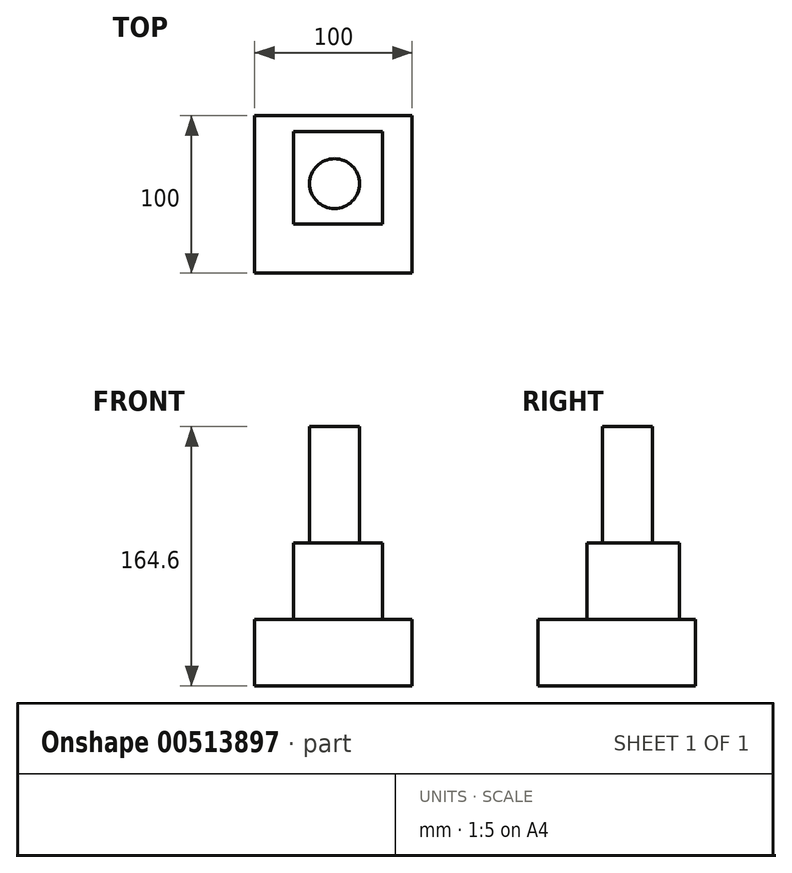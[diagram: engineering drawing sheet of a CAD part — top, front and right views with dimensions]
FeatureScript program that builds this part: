
annotation { "Feature Type Name" : "Feature", "Feature Type Description" : "" }
export const myFeature = defineFeature(function(context is Context, id is Id, definition is map)
    precondition{}
    {
        {
            var Q0;
            Q0=qCreatedBy(makeId("Top.planeOp"),FACE);
            var sketch = newSketch(context, id + "F0", { "sketchPlane" : qUnion([Q0])});
            skLineSegment(sketch, "E0.bottom", {"start": v(-50.73, 47.1) * mm, "end": v(49.27, 47.1) * mm});
            skLineSegment(sketch, "E0.top", {"start": v(-50.73, -52.9) * mm, "end": v(49.27, -52.9) * mm});
            skLineSegment(sketch, "E0.left", {"start": v(-50.73, 47.1) * mm, "end": v(-50.73, -52.9) * mm});
            skLineSegment(sketch, "E0.right", {"start": v(49.27, 47.1) * mm, "end": v(49.27, -52.9) * mm});
            skSolve(sketch);
        }
        {
            var Q0;
            Q0=makeQuery(id+"F0.imprint","IMPRINT",FACE,{"disambiguationData":[TD([[makeQuery(id+"F0.imprint","IMPRINT",EDGE,{"derivedFrom":sQuery(id+"F0.wireOp",EDGE,"E0.bottom")}),-1.0]])]});
            extrude(context, id + "F1", {"entities" : qUnion([Q0]), "depth" : 42 * mm});
        }
        {
            var Q0;
            Q0=makeQuery(id+"F1.opExtrude","CAP_FACE",FACE,{"disambiguationData":[OSD([sQuery(id+"F0.wireOp",EDGE,"E0.bottom"),sQuery(id+"F0.wireOp",EDGE,"E0.top"),sQuery(id+"F0.wireOp",EDGE,"E0.left"),sQuery(id+"F0.wireOp",EDGE,"E0.right")])],"isStart":false});
            var sketch = newSketch(context, id + "F2", { "sketchPlane" : qUnion([Q0])});
            skLineSegment(sketch, "E1.bottom", {"start": v(-26.06, 36.97) * mm, "end": v(30.42, 36.97) * mm});
            skLineSegment(sketch, "E1.top", {"start": v(-26.06, -21.84) * mm, "end": v(30.42, -21.84) * mm});
            skLineSegment(sketch, "E1.left", {"start": v(-26.06, 36.97) * mm, "end": v(-26.06, -21.84) * mm});
            skLineSegment(sketch, "E1.right", {"start": v(30.42, 36.97) * mm, "end": v(30.42, -21.84) * mm});
            skSolve(sketch);
        }
        {
            var Q0;
            Q0=makeQuery(id+"F2.imprint","IMPRINT",FACE,{"disambiguationData":[TD([[makeQuery(id+"F2.imprint","IMPRINT",EDGE,{"derivedFrom":sQuery(id+"F2.wireOp",EDGE,"E1.bottom")}),-1.0]])]});
            extrude(context, id + "F3", {"entities" : qUnion([Q0]), "operationType" : NewBodyOperationType.ADD, "depth" : 48.7 * mm});
        }
        {
            var Q0;
            Q0=makeQuery(id+"F3.opExtrude","CAP_FACE",FACE,{"disambiguationData":[OSD([sQuery(id+"F2.wireOp",EDGE,"E1.bottom"),sQuery(id+"F2.wireOp",EDGE,"E1.top"),sQuery(id+"F2.wireOp",EDGE,"E1.left"),sQuery(id+"F2.wireOp",EDGE,"E1.right")])],"isStart":false});
            var sketch = newSketch(context, id + "F4", { "sketchPlane" : qUnion([Q0])});
            skCircle(sketch, "E2", {"center": v(0, 3.95) * mm, "radius": 15.82 * mm});
            skSolve(sketch);
        }
        {
            var Q0;
            Q0 = qSketchRegion(id + "F4", true);
            extrude(context, id + "F5", {"entities" : qUnion([Q0]), "operationType" : NewBodyOperationType.ADD, "depth" : 73.9 * mm});
        }
        {
            var Q0;
            Q0 = qSketchRegion(id + "F0", true);
            extrude(context, id + "F6", {"entities" : qUnion([Q0]), "operationType" : NewBodyOperationType.ADD, "depth" : 25 * mm, "offsetDistance" : 25 * mm});
        }
    });
